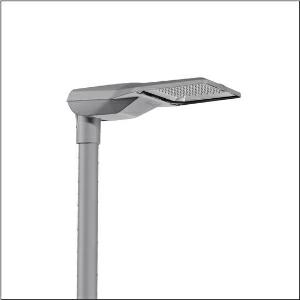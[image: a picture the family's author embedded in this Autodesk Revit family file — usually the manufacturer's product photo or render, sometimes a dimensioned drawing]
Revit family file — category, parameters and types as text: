
# Revit family: streetlight_sl_21_midi___stw1_0a_5xe7e43a08lb_4473
name_source: partatom
category: Lighting Fixtures
units: mm (PartAtom-declared; Revit-internal decimal feet)

## family parameters
Cut with Voids When Loaded = No
Host = Face
Light Source = No
Part Type = Normal
Room Calculation Point = No
Round Connector Dimension = Use Diameter
Shared = No

## types (1)
- --- (1 x LED, 14950 lm, 98.3 W, 4000K)
    Apparent Load = 98 VA
    CIE Flux Codes = 38 75 98 100 100
    Color Rendering = 70
    Color Temperature = 4000K
    Default Elevation = 1800 mm
    Description = Streetlight SL 21 midi, mast luminaire, primary light control with lens, of PMMA, primary optical cover: cover, of toughened safety glass, transparent, light distribution: STW1.0a, light emission: direct distribution, primary light characteristic: asymmetric, installation type: post-top, side-entry, LED, 3G 1.5mm², High Power LED, rated luminous flux: 14.950lm, luminous efficacy: 152lm/W, light colour: 740, colour temperature: 4000K, control: overheat protection, constant luminous flux control, time-dependent luminous flux control, flexible luminous flux parameterisation, mains connection: 220..240V, AC, 50/60Hz, connection cable pre-assembled, cable length: 10,5m, wiring characteristics: H07RN-F, start of lifetime: 98W, end of service life: 101W, reduction: 45W, luminaire housing, of diecast aluminium, powder-coated, Siteco® metallic grey (DB 702S), corrosivity category C5 mid according to DIN EN ISO 12944, please order mast flange separately, inclination adjustable: 0°, 5°, 10°, 15°, sealing non-destructively replaceable, multi-level sealing system, length: 644mm, width: 335mm, height: 110mm, mast flange for spigot size: 42mm (side-entry): 5XC10008XM4, 60/48mm (side-entry/post-top): 5XC10108XM2, 76/60mm (side-entry/post-top): 5XC10108XM1, protection rating (complete): IP66, insulation class (complete): insulation class II (safety insulation), certification: CE, ENEC, ENEC+, VDE, impact resistance: IK09, permissible operating ambient temperature for outdoor applications: -40..+50°C, standard-compliant lighting for roads and squares, packaging unit: 1 piece

Light Distribution: STW1.0a
    Height = 111 mm
    Lamp = 1 x LED
    Lamp Light Flux = 14950 lm
    Lamp Power = 98.3 W
    Lamp count = 1
    Length = 644 mm
    Luminous efficacy = 152 lm/W
    Manufacturer = Siteco
    ModVariant = No
    Model = 5XE7E43A08LB
    Number of Poles = 1
    OnlyDefault = Yes
    Power Factor = 1
    Product Name = Streetlight SL 21 midi | STW1.0a
    Product group = mast luminaire | pylon top
    ProductGroupID = 6100
    Protection Class = Protection class II
    Protection Degree = IP 66
    RLX_Detail_Level = 1
    RLX_Emergency_Light_Flux = 0 lm
    RLX_Emergency_Type = 0
    RLX_Emergency_Type_DB = No
    RlxData = <blob elided: 91145 chars, md5=2859a2a6>
    Socket = socket
    Standby Power = 0 W
    System Light Flux = 14950 lm
    System Power = 98 W
    Type Comments = factory setting: luminous flux: 100 % | Output Level: 100 % | 1020 mA
    Type Image = l_1004298.jpg
    URL = http://relux.com
    VarID = @adj_139581
    Voltage = 0 V
    Weight = 0.00 kg
    Width = 336 mm

## geometry (parser evidence)
native form markers: Blend x4, Sweep x12
no freeform markers — native parametric forms only
